# Revit family: LAMP_FIL 120 1162MM OPAL SUSPENDED
name_source: partatom
category: Luminarias
revit_build: Autodesk Revit 2018 (Build: 20190510_1515(x64)
units: mm (PartAtom-declared; Revit-internal decimal feet)

## family parameters
Anfitrión = Cara
Compartido = No
Corte con vacíos al cargar = No
Cota de conector redondo = Diámetro de uso
Origen de luz = Sí
Punto de cálculo de habitación = No
Tipo de pieza = Normal

## types (8) — shared parameters
CRI = 80
Cambio de temperatura de color de luz atenuada = <Ninguno>
Dimensions = 1162x120x92
Elevación por defecto = 1219 mm
Filtro de color = 16777215
Installation instructions = https://www.lamp.es
Insulation class = I
LED Lifetime = 96.000 L90B10
Lamp = HIGH POWER LED
Last update = 31/01/2022
Longitud de línea de emisión = 1162 mm  [stored 3.81234 ft]
MacAdam = 3
Manufacturer URL = http://www.lamp.es
Manufacturer country = Spain
Manufacturer name = LAMP
Material difusor = LAMP_PC Difusor Opal Fil
Material suspension = LAMP_Acero genérico
Model explanation = Availability of switching between accessories through visibility parameters when placed in a project.
Plum = 49 W
Power = 45 W
Power Supply = 220-240V 50/60Hz
Product URL = https://www.lamp.es
Product datasheet = http://www.lamp.es
Protection rating = IP20
Type = HI POWER PHILIPS
Weight = 4.19 kg
Ángulo de inclinación = -90.00°

## per-type parameters (varying)
| type | Archivo de red fotométrica | Efficacy | Finish | Gear | Material perfil | Product code |
| 5090LM 3000K DALI GREY | F121SF12HOOP830nG.IES | 104 lm/W | Gloss grey | DALI | LAMP_Aluminio Perfil Fil GR | F121SF12HOOP830DG |
| 5090LM 3000K DALI WHITE | F121SF12HOOP830nW.IES | 104 lm/W | Matte white RAL 9010 | DALI | LAMP_Aluminio Perfil Fil BL | F121SF12HOOP830DW |
| 5090LM 3000K  GREY | F121SF12HOOP830NG.IES | 104 lm/W | Gloss grey | Electronic | LAMP_Aluminio Perfil Fil GR | F121SF12HOOP830NG |
| 5090LM 3000K  WHITE | F121SF12HOOP830NW.IES | 104 lm/W | Matte white RAL 9010 | Electronic | LAMP_Aluminio Perfil Fil BL | F121SF12HOOP830NW |
| 5290LM 4000K DALI GREY | F121SF12HOOP840nG.IES | 108 lm/W | Gloss grey | DALI | LAMP_Aluminio Perfil Fil GR | F121SF12HOOP840DG |
| 5290LM 4000K DALI WHITE | F121SF12HOOP840nW.IES | 108 lm/W | Matte white RAL 9010 | DALI | LAMP_Aluminio Perfil Fil BL | F121SF12HOOP840DW |
| 5290LM 4000K  GREY | F121SF12HOOP840NG.IES | 108 lm/W | Gloss grey | Electronic | LAMP_Aluminio Perfil Fil GR | F121SF12HOOP840NG |
| 5290LM 4000K  WHITE | F121SF12HOOP840NW.IES | 108 lm/W | Matte white RAL 9010 | Electronic | LAMP_Aluminio Perfil Fil BL | F121SF12HOOP840NW |

note: [stored X ft] marks values corroborated as IEEE doubles in the binary element streams (Revit-internal decimal feet)
